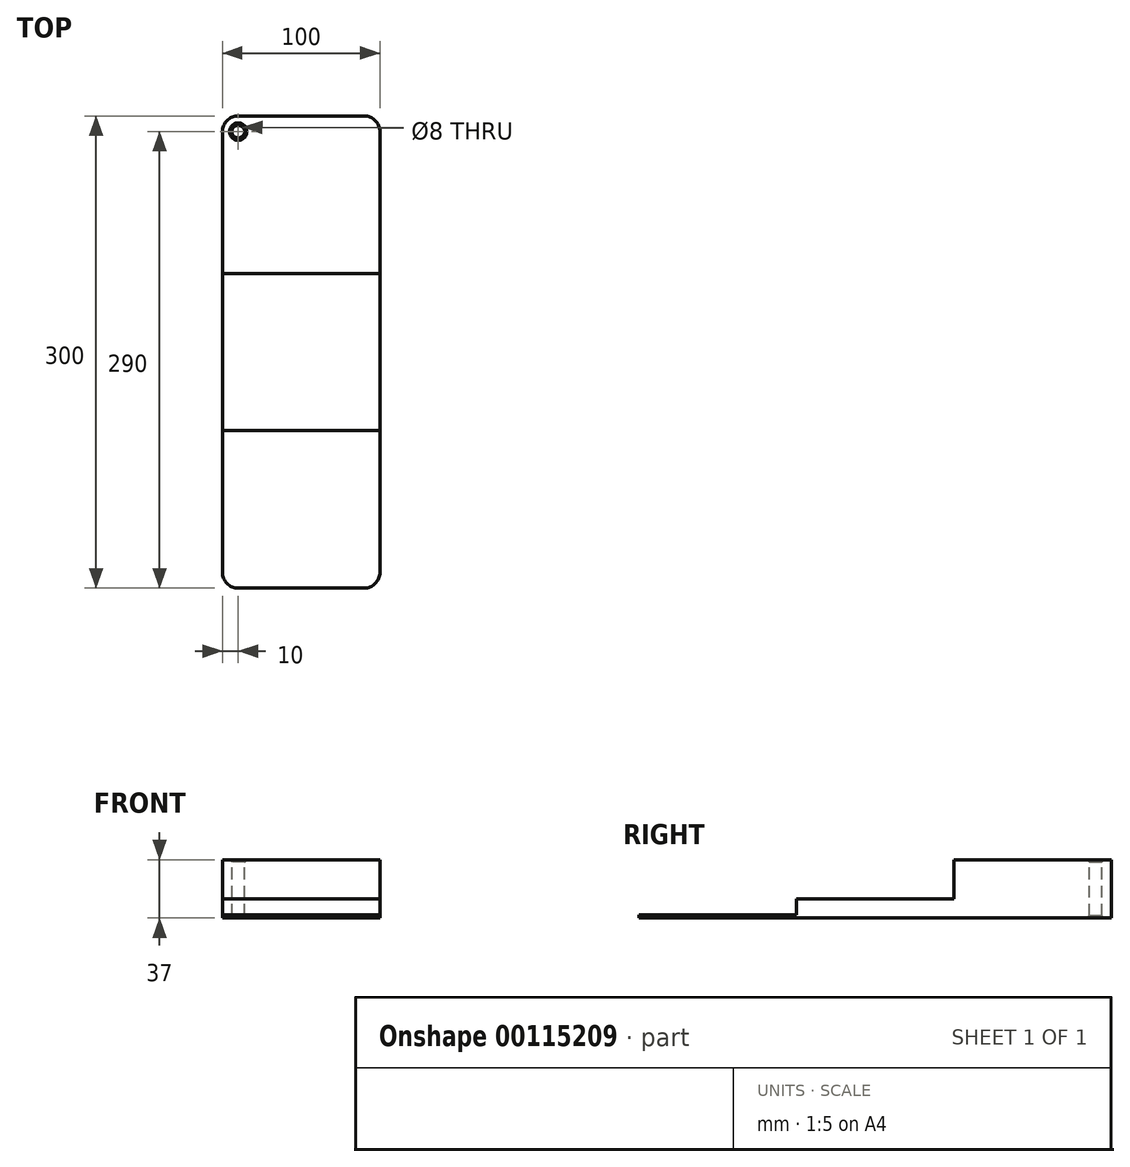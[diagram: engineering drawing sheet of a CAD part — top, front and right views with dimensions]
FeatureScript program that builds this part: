
annotation { "Feature Type Name" : "Feature", "Feature Type Description" : "" }
export const myFeature = defineFeature(function(context is Context, id is Id, definition is map)
    precondition{}
    {
        {
            var Q0;
            Q0=qCreatedBy(makeId("Top.planeOp"),FACE);
            var sketch = newSketch(context, id + "F0", { "sketchPlane" : qUnion([Q0])});
            skLineSegment(sketch, "E0.bottom", {"start": v(50, 150) * mm, "end": v(-50, 150) * mm});
            skLineSegment(sketch, "E0.top", {"start": v(50, -150) * mm, "end": v(-50, -150) * mm});
            skLineSegment(sketch, "E0.left", {"start": v(50, 150) * mm, "end": v(50, -150) * mm});
            skLineSegment(sketch, "E0.right", {"start": v(-50, 150) * mm, "end": v(-50, -150) * mm});
            skPoint(sketch, "E0.middle", {"position": v(0, 0) * mm});
            skSolve(sketch);
        }
        {
            var Q0;
            Q0 = qSketchRegion(id + "F0", true);
            extrude(context, id + "F1", {"entities" : qUnion([Q0]), "depth" : 2 * mm});
        }
        {
            var Q0;
            Q0=makeQuery(id+"F1.opExtrude","CAP_FACE",FACE,{"disambiguationData":[OSD([sQuery(id+"F0.wireOp",EDGE,"E0.bottom"),sQuery(id+"F0.wireOp",EDGE,"E0.top"),sQuery(id+"F0.wireOp",EDGE,"E0.left"),sQuery(id+"F0.wireOp",EDGE,"E0.right")])],"isStart":false});
            var sketch = newSketch(context, id + "F2", { "sketchPlane" : qUnion([Q0])});
            skLineSegment(sketch, "E1", {"start": v(-50, -50) * mm, "end": v(50, -50) * mm});
            skSolve(sketch);
        }
        {
            var Q0;
            {var subQ0=sQuery(id+"F2.wireOp",EDGE,"E1");Q0=makeQuery(id+"F2.imprint","IMPRINT",FACE,{"disambiguationData":[TD([[makeQuery(id+"F2.imprint","IMPRINT",EDGE,{"derivedFrom":subQ0}),1.0]])]});}
            extrude(context, id + "F3", {"entities" : qUnion([Q0]), "operationType" : NewBodyOperationType.ADD, "depth" : 10 * mm});
        }
        {
            var Q0;
            Q0=makeQuery(id+"F3.opExtrude","CAP_FACE",FACE,{"disambiguationData":[OSD([sQuery(id+"F0.wireOp",EDGE,"E0.bottom"),sQuery(id+"F0.wireOp",EDGE,"E0.left"),sQuery(id+"F0.wireOp",EDGE,"E0.right"),sQuery(id+"F2.wireOp",EDGE,"E1")])],"isStart":false});
            var sketch = newSketch(context, id + "F4", { "sketchPlane" : qUnion([Q0])});
            skLineSegment(sketch, "E2", {"start": v(-50, 50) * mm, "end": v(50, 50) * mm});
            skSolve(sketch);
        }
        {
            var Q0;
            {var subQ0=sQuery(id+"F4.wireOp",EDGE,"E2");Q0=makeQuery(id+"F4.imprint","IMPRINT",FACE,{"disambiguationData":[TD([[makeQuery(id+"F4.imprint","IMPRINT",EDGE,{"derivedFrom":subQ0}),1.0]])]});}
            extrude(context, id + "F5", {"entities" : qUnion([Q0]), "operationType" : NewBodyOperationType.ADD, "depth" : 25 * mm});
        }
        {
            var Q0;
            {var subQ0=sQuery(id+"F0.wireOp",EDGE,"E0.right");var subQ1=sQuery(id+"F0.wireOp",EDGE,"E0.bottom");Q0=makeQuery(id+"F5.boolean.opBoolean","MERGE",EDGE,{"derivedFrom":[makeQuery(id+"F3.boolean.opBoolean","MERGE",EDGE,{"derivedFrom":[makeQuery(id+"F1.opExtrude","SWEPT_EDGE",EDGE,{"disambiguationData":[OSD([subQ1,subQ0])]}),makeQuery(id+"F3.opExtrude","SWEPT_EDGE",EDGE,{"disambiguationData":[OSD([subQ1,subQ0])]})]}),makeQuery(id+"F5.opExtrude","SWEPT_EDGE",EDGE,{"disambiguationData":[OSD([subQ1,subQ0])]})]});}
            var Q1;
            Q1=makeQuery(id+"F1.opExtrude","SWEPT_EDGE",EDGE,{"disambiguationData":[OSD([sQuery(id+"F0.wireOp",EDGE,"E0.top"),sQuery(id+"F0.wireOp",EDGE,"E0.right")])]});
            var Q2;
            Q2=makeQuery(id+"F1.opExtrude","SWEPT_EDGE",EDGE,{"disambiguationData":[OSD([sQuery(id+"F0.wireOp",EDGE,"E0.top"),sQuery(id+"F0.wireOp",EDGE,"E0.left")])]});
            var Q3;
            {var subQ0=sQuery(id+"F0.wireOp",EDGE,"E0.left");var subQ1=sQuery(id+"F0.wireOp",EDGE,"E0.bottom");Q3=makeQuery(id+"F5.boolean.opBoolean","MERGE",EDGE,{"derivedFrom":[makeQuery(id+"F3.boolean.opBoolean","MERGE",EDGE,{"derivedFrom":[makeQuery(id+"F1.opExtrude","SWEPT_EDGE",EDGE,{"disambiguationData":[OSD([subQ1,subQ0])]}),makeQuery(id+"F3.opExtrude","SWEPT_EDGE",EDGE,{"disambiguationData":[OSD([subQ1,subQ0])]})]}),makeQuery(id+"F5.opExtrude","SWEPT_EDGE",EDGE,{"disambiguationData":[OSD([subQ1,subQ0])]})]});}
            fillet(context, id + "F6", {"entities" : qUnion([Q0, Q1, Q2, Q3]), "radius" : 10 * mm, "tangentPropagation" : true, "allowEdgeOverflow" : false});
        }
        {
            var Q0;
            Q0=makeQuery(id+"F5.opExtrude","CAP_FACE",FACE,{"disambiguationData":[OSD([sQuery(id+"F0.wireOp",EDGE,"E0.bottom"),sQuery(id+"F0.wireOp",EDGE,"E0.left"),sQuery(id+"F0.wireOp",EDGE,"E0.right"),sQuery(id+"F4.wireOp",EDGE,"E2")])],"isStart":false});
            var sketch = newSketch(context, id + "F7", { "sketchPlane" : qUnion([Q0])});
            skCircle(sketch, "E3", {"center": v(-40, 140) * mm, "radius": 4 * mm});
            skSolve(sketch);
        }
        {
            var Q0;
            Q0 = qSketchRegion(id + "F7", true);
            extrude(context, id + "F8", {"entities" : qUnion([Q0]), "operationType" : NewBodyOperationType.REMOVE, "endBound" : BoundingType.THROUGH_ALL, "oppositeDirection" : true, "depth" : 25 * mm});
        }
        {
            var Q0;
            Q0=makeQuery(id+"F8.boolean.opBoolean","COPY",FACE,{"derivedFrom":makeQuery(id+"F8.opExtrude","SWEPT_FACE",FACE,{"disambiguationData":[OSD([sQuery(id+"F7.wireOp",EDGE,"E3")])]})});
            chamfer(context, id + "F9", {"entities" : qUnion([Q0]), "width" : 1.5 * mm, "tangentPropagation" : true});
        }
    });
